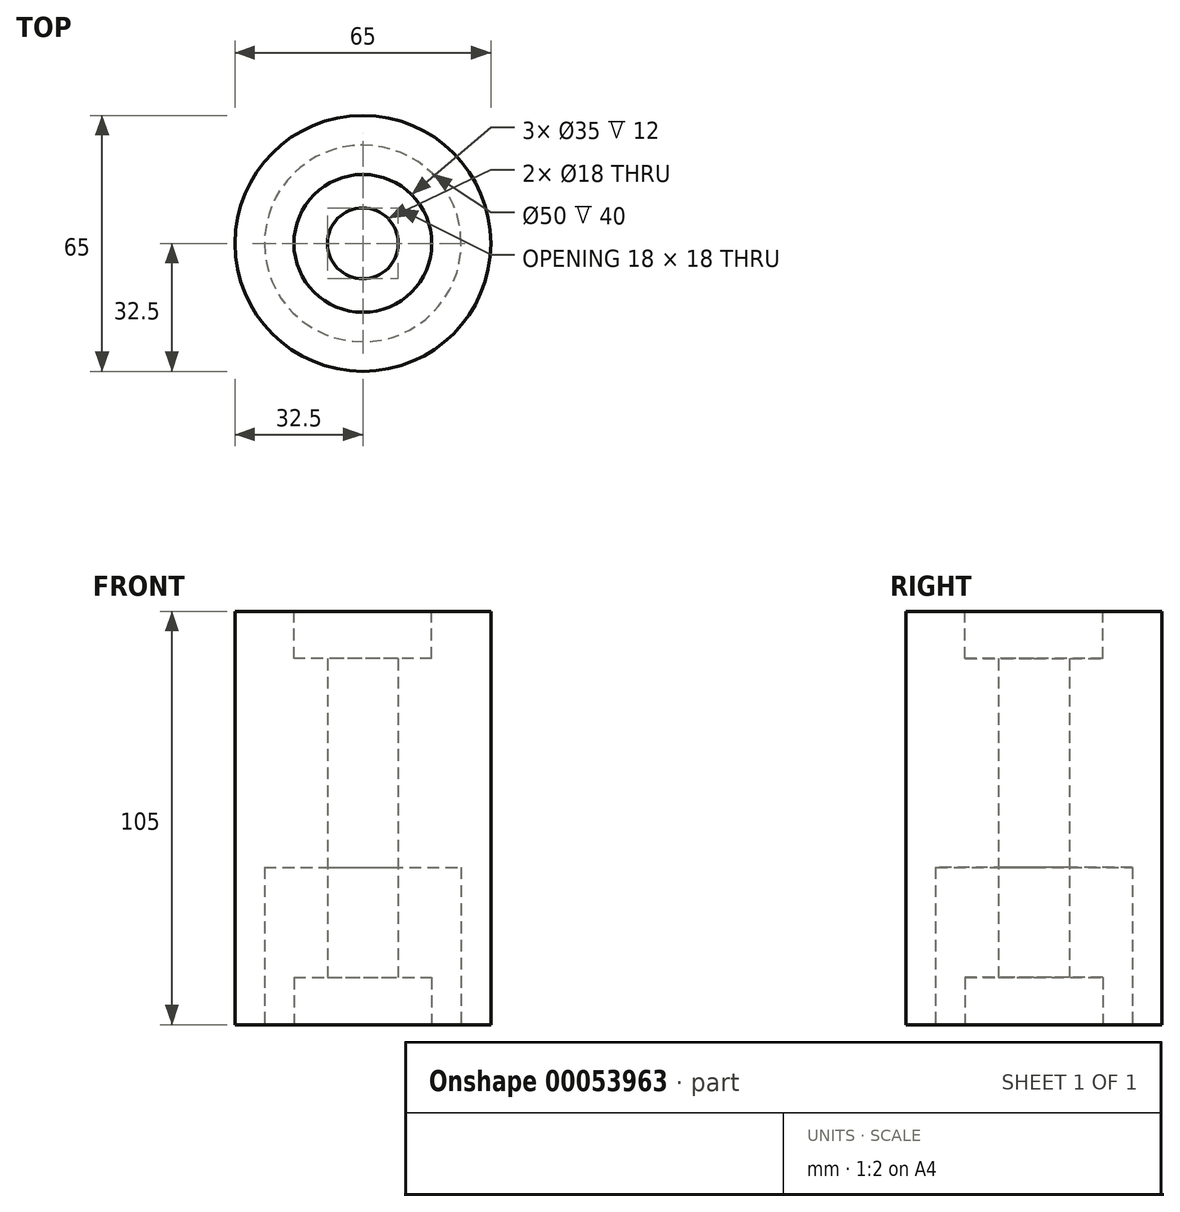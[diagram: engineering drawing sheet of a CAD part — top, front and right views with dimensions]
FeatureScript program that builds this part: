
annotation { "Feature Type Name" : "Feature", "Feature Type Description" : "" }
export const myFeature = defineFeature(function(context is Context, id is Id, definition is map)
    precondition{}
    {
        {
            var Q0;
            Q0=qCreatedBy(makeId("Top.planeOp"),FACE);
            var sketch = newSketch(context, id + "F0", { "sketchPlane" : qUnion([Q0])});
            skCircle(sketch, "E0", {"center": v(0, 0) * mm, "radius": 32.5 * mm});
            skSolve(sketch);
        }
        {
            var Q0;
            Q0=makeQuery(id+"F0.imprint","IMPRINT",FACE,{"disambiguationData":[TD([[makeQuery(id+"F0.imprint","IMPRINT",EDGE,{"derivedFrom":sQuery(id+"F0.wireOp",EDGE,"E0")}),1.0]])]});
            extrude(context, id + "F1", {"entities" : qUnion([Q0]), "depth" : 105 * mm});
        }
        {
            var Q0;
            Q0=makeQuery(id+"F1.opExtrude","CAP_FACE",FACE,{"disambiguationData":[OSD([sQuery(id+"F0.wireOp",EDGE,"E0")])],"isStart":false});
            var sketch = newSketch(context, id + "F2", { "sketchPlane" : qUnion([Q0])});
            skCircle(sketch, "E1", {"center": v(0, 0) * mm, "radius": 7 * mm});
            skPoint(sketch, "E2.rect.middle", {"position": v(0, 7) * mm});
            skSolve(sketch);
        }
        {
            var Q0;
            Q0 = qSketchRegion(id + "F2", true);
            extrude(context, id + "F3", {"entities" : qUnion([Q0]), "operationType" : NewBodyOperationType.REMOVE, "oppositeDirection" : true, "depth" : 110 * mm});
        }
        {
            var Q0;
            Q0=makeQuery(id+"F1.opExtrude","CAP_FACE",FACE,{"disambiguationData":[OSD([sQuery(id+"F0.wireOp",EDGE,"E0")])],"isStart":true});
            var sketch = newSketch(context, id + "F4", { "sketchPlane" : qUnion([Q0])});
            skCircle(sketch, "E3", {"center": v(0, 0) * mm, "radius": 25 * mm});
            skSolve(sketch);
        }
        {
            var Q0;
            Q0 = qSketchRegion(id + "F4", true);
            extrude(context, id + "F5", {"entities" : qUnion([Q0]), "operationType" : NewBodyOperationType.REMOVE, "oppositeDirection" : true, "depth" : 40 * mm});
        }
        {
            var Q0;
            Q0=makeQuery(id+"F1.opExtrude","CAP_FACE",FACE,{"disambiguationData":[OSD([sQuery(id+"F0.wireOp",EDGE,"E0")])],"isStart":false});
            var sketch = newSketch(context, id + "F6", { "sketchPlane" : qUnion([Q0])});
            skPoint(sketch, "E4", {"position": v(0, 32.5) * mm});
            skSolve(sketch);
        }
        {
            var Q0;
            Q0 = qSketchRegion(id + "F0", true);
            extrude(context, id + "F7", {"entities" : qUnion([Q0]), "depth" : 105 * mm});
        }
        {
            var Q0;
            Q0=makeQuery(id+"F7.opExtrude","CAP_FACE",FACE,{"disambiguationData":[OSD([sQuery(id+"F0.wireOp",EDGE,"E0")])],"isStart":true});
            var sketch = newSketch(context, id + "F8", { "sketchPlane" : qUnion([Q0])});
            skCircle(sketch, "E5", {"center": v(0, 0) * mm, "radius": 9 * mm});
            skSolve(sketch);
        }
        {
            var Q0;
            Q0=makeQuery(id+"F8.imprint","IMPRINT",FACE,{"disambiguationData":[TD([[makeQuery(id+"F8.imprint","IMPRINT",EDGE,{"derivedFrom":sQuery(id+"F8.wireOp",EDGE,"E5")}),1.0]])]});
            extrude(context, id + "F9", {"entities" : qUnion([Q0]), "operationType" : NewBodyOperationType.REMOVE, "oppositeDirection" : true, "depth" : 105 * mm});
        }
        {
            var Q0;
            Q0=makeQuery(id+"F7.opExtrude","CAP_FACE",FACE,{"disambiguationData":[OSD([sQuery(id+"F0.wireOp",EDGE,"E0")])],"isStart":true});
            var sketch = newSketch(context, id + "F10", { "sketchPlane" : qUnion([Q0])});
            skCircle(sketch, "E6", {"center": v(0, 0) * mm, "radius": 17.5 * mm});
            skSolve(sketch);
        }
        {
            var Q0;
            Q0 = qSketchRegion(id + "F10", true);
            var Q1;
            Q1=makeQuery(id+"F10.imprint","IMPRINT",FACE,{"disambiguationData":[TD([[makeQuery(id+"F10.imprint","IMPRINT",EDGE,{"derivedFrom":sQuery(id+"F10.wireOp",EDGE,"E6")}),1.0]])]});
            extrude(context, id + "F11", {"entities" : qUnion([Q0, Q1]), "operationType" : NewBodyOperationType.REMOVE, "oppositeDirection" : true, "depth" : 12 * mm});
        }
        {
            var Q0;
            Q0=makeQuery(id+"F6.imprint","IMPRINT",FACE,{"disambiguationData":[TD([[makeQuery(id+"F6.imprint","IMPRINT",EDGE,{"derivedFrom":makeQuery(id+"F1.opExtrude","CAP_EDGE",EDGE,{"disambiguationData":[OSD([sQuery(id+"F0.wireOp",EDGE,"E0")])],"isStart":false})}),1.0]])]});
            var sketch = newSketch(context, id + "F12", { "sketchPlane" : qUnion([Q0])});
            skCircle(sketch, "E7", {"center": v(0, 0) * mm, "radius": 17.5 * mm});
            skSolve(sketch);
        }
        {
            var Q0;
            Q0 = qSketchRegion(id + "F12", true);
            extrude(context, id + "F13", {"entities" : qUnion([Q0]), "operationType" : NewBodyOperationType.REMOVE, "oppositeDirection" : true, "depth" : 12 * mm});
        }
    });
